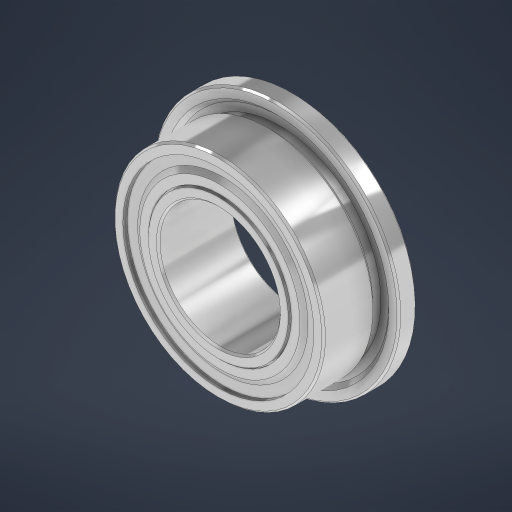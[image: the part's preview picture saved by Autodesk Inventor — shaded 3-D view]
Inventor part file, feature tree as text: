
AUTODESK INVENTOR PART (.ipt)
format: ipt  version: 2024 (Build 280153000, 153)  size: 790,016 bytes
history: native  units: in
note: dims shown in document units (in); Inventor stores cm internally (conversion verified against a paired STEP export)
features: other x14, revolve x3
ambient origin geometry x8: Origin, YZ Plane, XZ Plane, XY Plane, X Axis, Y Axis, Z Axis, Center Point
bodies: Solid1 (feature_tree), Solid2 (feature_tree), Solid3 (feature_tree), Solid4 (feature_tree), Solid5 (feature_tree), Solid6 (feature_tree), Solid7 (feature_tree), Solid8 (feature_tree), Solid9 (feature_tree), Solid10 (feature_tree), Solid11 (feature_tree), Solid12 (feature_tree), Solid13 (feature_tree), Solid14 (feature_tree), Solid15 (feature_tree), Solid16 (feature_tree), Solid17 (feature_tree)
feature tree (17):
  revolve  "Revolve3"  [1 undecoded]
  other  "CirPattern3[1]"
  other  "CirPattern3[2]"
  other  "CirPattern3[3]"
  other  "CirPattern3[4]"
  other  "CirPattern3[5]"
  other  "CirPattern3[6]"
  other  "CirPattern3[7]"
  other  "CirPattern3[8]"
  other  "CirPattern3[9]"
  other  "CirPattern3[10]"
  other  "CirPattern3[11]"
  other  "Cut-Revolve1[1]"
  other  "Cut-Revolve1[2]"
  revolve  "Revolve4[1]"  [1 undecoded]
  revolve  "Revolve4[2]"  [1 undecoded]
  other  "CirPattern3[12]"
note: 3 required parameter values undecoded (feature->parameter linkage not recoverable at this tier; creation-order binding heuristic only, values carry confidence <= 0.55)
